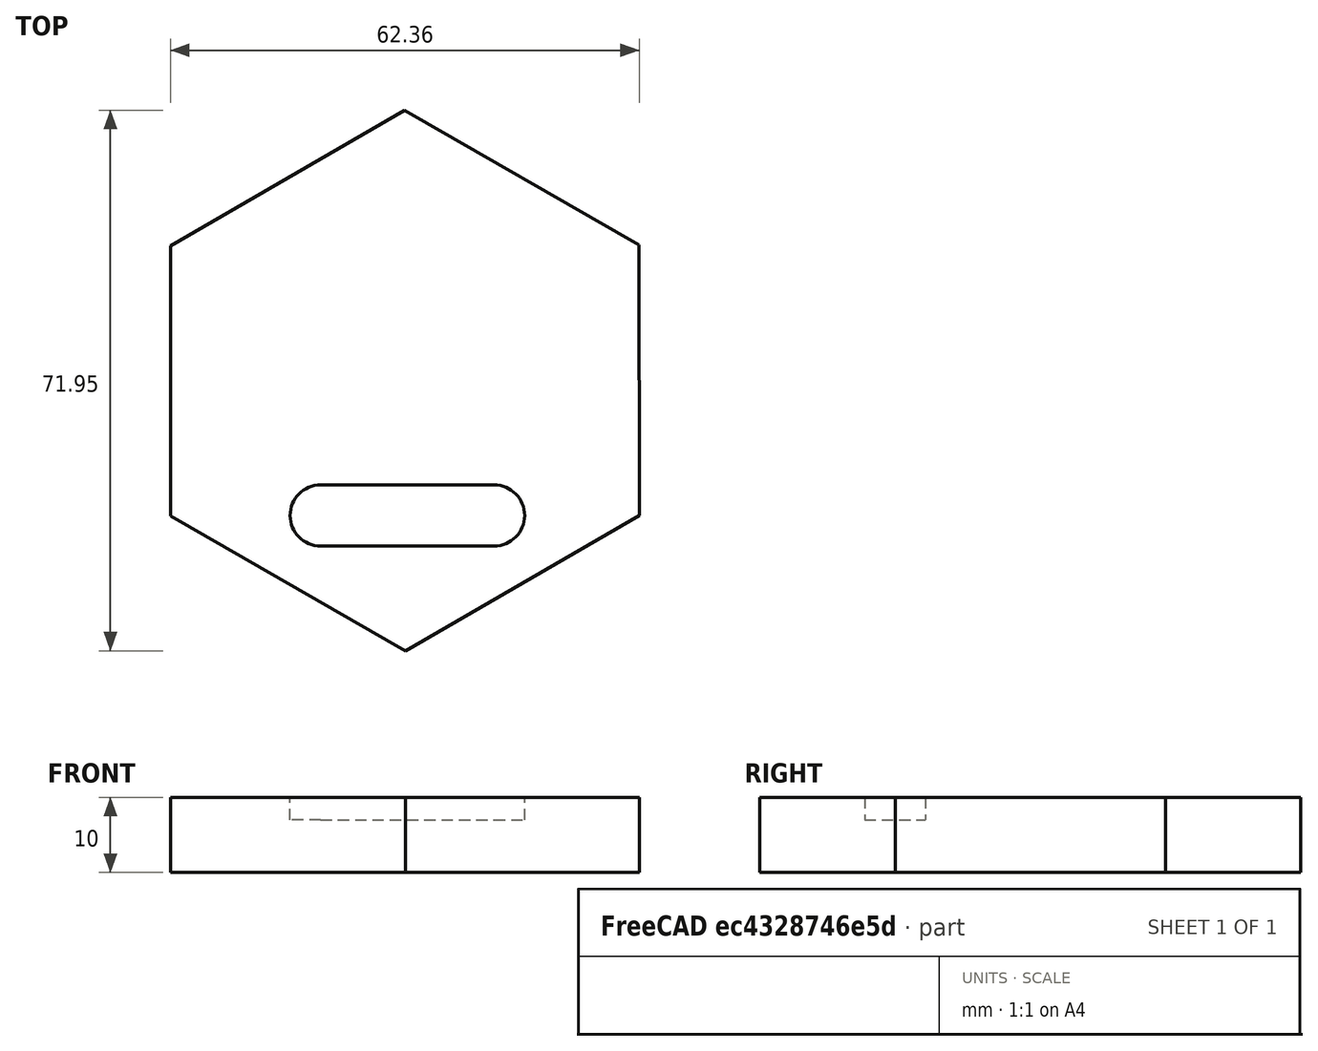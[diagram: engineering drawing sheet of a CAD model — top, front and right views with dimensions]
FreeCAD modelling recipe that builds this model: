
FCSTD DOCUMENT  (FreeCAD 1.0R38642 (Git))
Label: Opgave_1.1.3
License: All rights reserved
LicenseURL: http://en.wikipedia.org/wiki/All_rights_reserved
objects: Sketcher::SketchObject×1, PartDesign::Pad×1, PartDesign::Pocket×1, PartDesign::Body×1
note: 9 computed .brp shape members not serialized (recipe doc carries the construction recipe); baked Part::Feature solids carry a one-line shape summary decoded from their .brp

FEATURE [Sketcher::SketchObject] Sketch
  ArcFitTolerance = 1e-06
  AttachmentSupport = -> [XY_Plane]
  FullyConstrained = false
  MakeInternals = false
  MapMode = 5
  sketch-geometry (17):
    g0: LineSegment StartX=96.7236 StartY=31.1383 StartZ=0 EndX=96.6741 EndY=67.1161 EndZ=0
    g1: LineSegment StartX=96.6741 StartY=67.1161 StartZ=0 EndX=65.4917 EndY=85.0621 EndZ=0
    g2: LineSegment StartX=65.4917 StartY=85.0621 StartZ=0 EndX=34.3588 EndY=67.0304 EndZ=0
    g3: LineSegment StartX=34.3588 StartY=67.0304 StartZ=0 EndX=34.4083 EndY=31.0527 EndZ=0
    g4: LineSegment StartX=34.4083 StartY=31.0527 StartZ=0 EndX=65.5907 EndY=13.1066 EndZ=0
    g5: LineSegment StartX=65.5907 StartY=13.1066 StartZ=0 EndX=96.7236 EndY=31.1383 EndZ=0
    g6: Circle [constr] CenterX=65.5412 CenterY=49.0844 CenterZ=0 NormalX=0 NormalY=0 NormalZ=1 AngleXU=0 Radius=35.9778
    g7: Circle CenterX=50.0453 CenterY=61.4527 CenterZ=0 NormalX=0 NormalY=0 NormalZ=1 AngleXU=0 Radius=4.61885
    g8: Circle CenterX=80.0827 CenterY=61.986 CenterZ=0 NormalX=0 NormalY=0 NormalZ=1 AngleXU=0 Radius=5.15796
    g9: ArcOfCircle CenterX=54.3254 CenterY=31.1269 CenterZ=0 NormalX=0 NormalY=0 NormalZ=1 AngleXU=0 Radius=4.05549 StartAngle=1.5708 EndAngle=4.71239
    g10: ArcOfCircle CenterX=77.4117 CenterY=31.1269 CenterZ=0 NormalX=0 NormalY=0 NormalZ=1 AngleXU=0 Radius=4.05549 StartAngle=4.71239 EndAngle=7.85398
    g11: LineSegment StartX=54.3254 StartY=35.1823 StartZ=0 EndX=77.4117 EndY=35.1823 EndZ=0
    g12: LineSegment StartX=54.3254 StartY=27.0714 StartZ=0 EndX=77.4117 EndY=27.0714 EndZ=0
    g13: LineSegment StartX=65.5538 StartY=55.2965 StartZ=0 EndX=60.155 EndY=45.9892 EndZ=0
    g14: LineSegment StartX=60.155 StartY=45.9892 StartZ=0 EndX=70.9148 EndY=45.9674 EndZ=0
    g15: LineSegment StartX=70.9148 StartY=45.9674 StartZ=0 EndX=65.5538 EndY=55.2965 EndZ=0
    g16: Circle [constr] CenterX=65.5412 CenterY=49.0844 CenterZ=0 NormalX=0 NormalY=0 NormalZ=1 AngleXU=0 Radius=6.21217
  constraints (28):
    c: Coincident(g0,g1)
    c: Coincident(g1,g2)
    c: Coincident(g2,g3)
    c: Coincident(g3,g4)
    c: Coincident(g4,g5)
    c: Coincident(g5,g0)
    c: Equal(g0, g1-g5) x5
    c: PointOnObject(g0,g6)
    c: PointOnObject(g1,g6)
    c: PointOnObject(g2,g6)
    c: PointOnObject(g3,g6)
    c: PointOnObject(g4,g6)
    c: PointOnObject(g5,g6)
    c: Tangent(g9,g11) = 1.5708
    c: Tangent(g9,g12) = -1.5708
    c: Tangent(g10,g11) = 1.5708
    c: Tangent(g10,g12) = -1.5708
    c: Equal(g9,g10)
    c: Horizontal(g12)
    c: Coincident(g13,g14)
    c: Coincident(g14,g15)
    c: Coincident(g15,g13)
    c: Equal(g13,g14)
    c: Equal(g13,g15)
    c: PointOnObject(g13,g16)
    c: PointOnObject(g14,g16)
    c: PointOnObject(g15,g16)
    c: Coincident(g6,g16)
FEATURE [PartDesign::Pad] Pad
  Direction = (0,0,1)
  Length = 10
  Length2 = 10
  Profile = -> Sketch [Edge4,Edge3,Edge2,Edge1,Edge6,Edge5]
  ReferenceAxis = -> Sketch [N_Axis]
  Refine = true
  Reversed = true
  Suppressed = false
  Type = 0
FEATURE [PartDesign::Pocket] Pocket
  BaseFeature = -> Pad
  Direction = (0,0,-1)
  Length = 3
  Length2 = 5
  Profile = -> Sketch [Edge10,Edge12,Edge9,Edge11]
  ReferenceAxis = -> Sketch [N_Axis]
  Refine = true
  Suppressed = false
  Type = 0
FEATURE [PartDesign::Body] Body
  AllowCompound = true
  Group = -> [Sketch,Pad,Pocket]
  Origin = -> Origin
  Tip = -> Pocket
